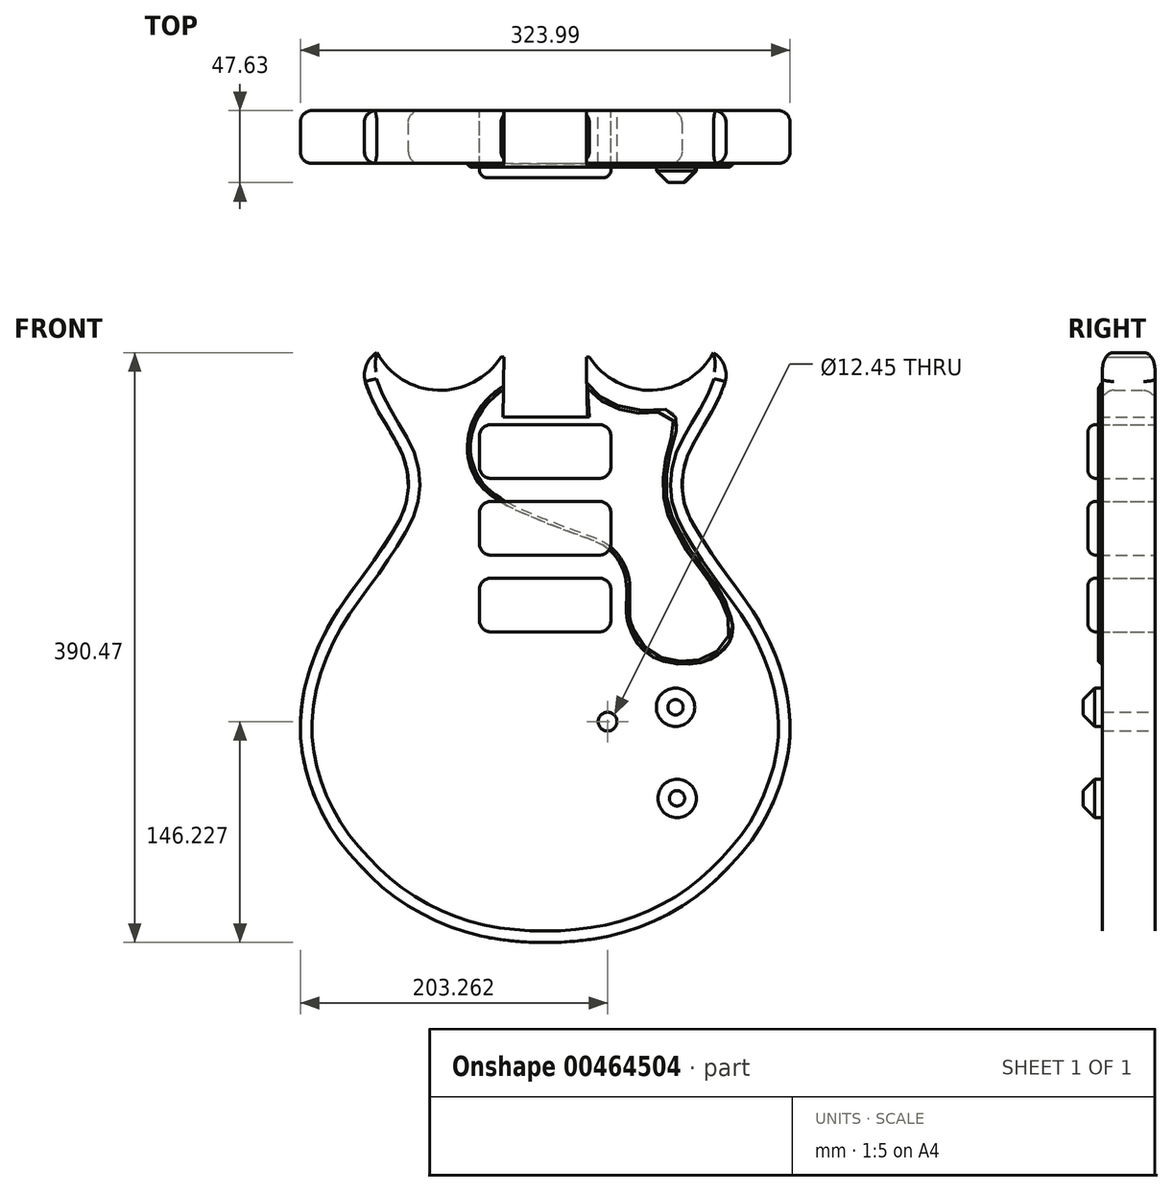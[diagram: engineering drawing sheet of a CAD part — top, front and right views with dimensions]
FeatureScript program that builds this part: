
annotation { "Feature Type Name" : "Feature", "Feature Type Description" : "" }
export const myFeature = defineFeature(function(context is Context, id is Id, definition is map)
    precondition{}
    {
        {
            var Q0;
            Q0=qCreatedBy(makeId("Front.planeOp"),FACE);
            var sketch = newSketch(context, id + "F0", { "sketchPlane" : qUnion([Q0])});
            skLineSegment(sketch, "E0", {"start": v(160.42, -4.78) * mm, "end": v(160.42, -171.98) * mm, "construction": true});
            skPoint(sketch, "E1", {"position": v(-1.5, 235.63) * mm});
            skLineSegment(sketch, "E2", {"start": v(-163.43, -5.5) * mm, "end": v(160.42, -5.5) * mm});
            skFitSpline(sketch, "E3", {"points": [v(-1.5, -151.72) * mm, v(45.27, -146.37) * mm, v(94.86, -123.83) * mm, v(121.95, -99.6) * mm, v(140.43, -76.25) * mm, v(156.45, -39.05) * mm, v(160.42, -5.5) * mm, v(154.1, 29.55) * mm, v(138.6, 63.2) * mm, v(123.42, 85.1) * mm, v(106.27, 109.26) * mm, v(94.33, 129.17) * mm, v(90.62, 138.56) * mm, v(89.22, 146.97) * mm, v(89.22, 156.81) * mm, v(91.97, 168.61) * mm, v(96.1, 177.88) * mm, v(102.04, 187.96) * mm, v(117.66, 219.62) * mm], "startDerivative": vector(474.35, 0.52) * mm, "endDerivative": vector(103.92, 419.42) * mm});
            skLineSegment(sketch, "E4", {"start": v(-1.5, 235.63) * mm, "end": v(27.7, 235.63) * mm});
            skLineSegment(sketch, "E5", {"start": v(-1.5, 235.63) * mm, "end": v(-30.71, 235.63) * mm});
            skArc(sketch, "E6", {"start": v(117.66, 219.62) * mm, "mid": v(116.83, 230.43) * mm, "end": v(109.86, 238.75) * mm});
            skArc(sketch, "E7", {"start": v(27.7, 235.63) * mm, "mid": v(69.67, 213.82) * mm, "end": v(109.86, 238.75) * mm});
            skArc(sketch, "E8.MirrorCS", {"start": v(-30.71, 235.63) * mm, "mid": v(-72.68, 213.82) * mm, "end": v(-112.87, 238.75) * mm});
            skArc(sketch, "E9.MirrorCS", {"start": v(-120.66, 219.62) * mm, "mid": v(-119.83, 230.43) * mm, "end": v(-112.87, 238.75) * mm});
            skPoint(sketch, "E10", {"position": v(-1.5, 80.55) * mm});
            skPoint(sketch, "E11", {"position": v(-1.5, 99.8) * mm});
            skPoint(sketch, "E12", {"position": v(-1.5, 175.58) * mm});
            skPoint(sketch, "E13", {"position": v(-1.5, 194.73) * mm});
            skPoint(sketch, "E14", {"position": v(109.79, 201.35) * mm});
            skPoint(sketch, "E15", {"position": v(-1.5, -5.67) * mm});
            skFitSpline(sketch, "E16.MirrorCS", {"points": [v(-1.5, -151.72) * mm, v(-48.27, -146.37) * mm, v(-97.86, -123.83) * mm, v(-122.77, -101.9) * mm, v(-143.44, -76.25) * mm, v(-159.45, -39.05) * mm, v(-163.43, -5.5) * mm, v(-157.11, 29.55) * mm, v(-141.6, 63.2) * mm, v(-126.43, 85.1) * mm, v(-109.28, 109.26) * mm, v(-97.34, 129.17) * mm, v(-93.62, 138.56) * mm, v(-92.23, 146.97) * mm, v(-92.23, 156.81) * mm, v(-94.98, 168.61) * mm, v(-99.1, 177.88) * mm, v(-105.05, 187.96) * mm, v(-120.66, 219.62) * mm], "startDerivative": vector(-474.35, 0.52) * mm, "endDerivative": vector(-103.92, 419.42) * mm});
            skPoint(sketch, "E17", {"position": v(30.82, 231.35) * mm});
            skCircle(sketch, "E18", {"center": v(-42.78, -5.5) * mm, "radius": 6.22 * mm});
            skCircle(sketch, "E19", {"center": v(39.77, -5.5) * mm, "radius": 6.22 * mm});
            skLineSegment(sketch, "E20", {"start": v(-1.5, 31.8) * mm, "end": v(-1.5, 657.27) * mm});
            skPoint(sketch, "E21", {"position": v(-1.5, 196) * mm});
            skLineSegment(sketch, "E22", {"start": v(-1.5, 196) * mm, "end": v(26.44, 196) * mm});
            skLineSegment(sketch, "E23", {"start": v(26.44, 196) * mm, "end": v(-1.5, 196) * mm});
            skLineSegment(sketch, "E24", {"start": v(-1.5, 196) * mm, "end": v(-29.44, 196) * mm});
            skLineSegment(sketch, "E25", {"start": v(-1.5, 657.27) * mm, "end": v(-22.14, 657.27) * mm});
            skLineSegment(sketch, "E26", {"start": v(-1.5, 657.27) * mm, "end": v(19.13, 657.27) * mm});
            skLineSegment(sketch, "E27", {"start": v(19.13, 657.27) * mm, "end": v(26.44, 196) * mm});
            skLineSegment(sketch, "E28", {"start": v(-29.44, 196) * mm, "end": v(-22.14, 657.27) * mm});
            skLineSegment(sketch, "E29", {"start": v(-1.5, 31.8) * mm, "end": v(87.54, 31.8) * mm});
            skLineSegment(sketch, "E30.bottom", {"start": v(-37.38, 140.28) * mm, "end": v(34.37, 140.28) * mm});
            skLineSegment(sketch, "E30.top", {"start": v(-37.38, 104.72) * mm, "end": v(34.37, 104.72) * mm});
            skLineSegment(sketch, "E30.left", {"start": v(-45, 132.66) * mm, "end": v(-45, 112.34) * mm});
            skLineSegment(sketch, "E30.right", {"start": v(42, 132.66) * mm, "end": v(42, 112.34) * mm});
            skPoint(sketch, "E31.visualSharp", {"position": v(-45, 140.28) * mm});
            skArc(sketch, "E31.filletArc", {"start": v(-37.38, 140.28) * mm, "mid": v(-42.77, 138.05) * mm, "end": v(-45, 132.66) * mm});
            skPoint(sketch, "E32.visualSharp", {"position": v(42, 140.28) * mm});
            skArc(sketch, "E32.filletArc", {"start": v(42, 132.66) * mm, "mid": v(39.76, 138.05) * mm, "end": v(34.37, 140.28) * mm});
            skPoint(sketch, "E33.visualSharp", {"position": v(42, 104.72) * mm});
            skArc(sketch, "E33.filletArc", {"start": v(34.37, 104.72) * mm, "mid": v(39.76, 106.95) * mm, "end": v(42, 112.34) * mm});
            skPoint(sketch, "E34.visualSharp", {"position": v(-45, 104.72) * mm});
            skArc(sketch, "E34.filletArc", {"start": v(-45, 112.34) * mm, "mid": v(-42.77, 106.95) * mm, "end": v(-37.38, 104.72) * mm});
            skLineSegment(sketch, "E35", {"start": v(-1.5, 140.28) * mm, "end": v(-1.5, 104.72) * mm, "construction": true});
            skLineSegment(sketch, "E36", {"start": v(-45, 122.5) * mm, "end": v(42, 122.5) * mm, "construction": true});
            skLineSegment(sketch, "E37.bottom", {"start": v(-37.38, 191.08) * mm, "end": v(34.37, 191.08) * mm});
            skLineSegment(sketch, "E37.top", {"start": v(-37.38, 155.52) * mm, "end": v(34.37, 155.52) * mm});
            skLineSegment(sketch, "E37.left", {"start": v(-45, 183.46) * mm, "end": v(-45, 163.14) * mm});
            skLineSegment(sketch, "E37.right", {"start": v(42, 183.46) * mm, "end": v(42, 163.14) * mm});
            skPoint(sketch, "E38.visualSharp", {"position": v(-45, 186.25) * mm});
            skArc(sketch, "E38.filletArc", {"start": v(-37.38, 191.08) * mm, "mid": v(-42.77, 188.85) * mm, "end": v(-45, 183.46) * mm});
            skPoint(sketch, "E39.visualSharp", {"position": v(42, 186.25) * mm});
            skArc(sketch, "E39.filletArc", {"start": v(42, 183.46) * mm, "mid": v(39.76, 188.85) * mm, "end": v(34.37, 191.08) * mm});
            skPoint(sketch, "E40.visualSharp", {"position": v(42, 155.52) * mm});
            skArc(sketch, "E40.filletArc", {"start": v(34.37, 155.52) * mm, "mid": v(39.76, 157.75) * mm, "end": v(42, 163.14) * mm});
            skPoint(sketch, "E41.visualSharp", {"position": v(-45, 155.52) * mm});
            skArc(sketch, "E41.filletArc", {"start": v(-45, 163.14) * mm, "mid": v(-42.77, 157.75) * mm, "end": v(-37.38, 155.52) * mm});
            skLineSegment(sketch, "E42", {"start": v(-1.5, 186.25) * mm, "end": v(-1.5, 150.7) * mm, "construction": true});
            skLineSegment(sketch, "E43", {"start": v(-45, 173.3) * mm, "end": v(42, 173.3) * mm, "construction": true});
            skPoint(sketch, "E44", {"position": v(-1.5, 173.3) * mm});
            skPoint(sketch, "E45", {"position": v(-1.5, 122.5) * mm});
            skLineSegment(sketch, "E46.bottom", {"start": v(-37.38, 89.48) * mm, "end": v(34.37, 89.48) * mm});
            skLineSegment(sketch, "E46.top", {"start": v(-37.38, 53.92) * mm, "end": v(34.37, 53.92) * mm});
            skLineSegment(sketch, "E46.left", {"start": v(-45, 81.86) * mm, "end": v(-45, 61.54) * mm});
            skLineSegment(sketch, "E46.right", {"start": v(42, 81.86) * mm, "end": v(42, 61.54) * mm});
            skPoint(sketch, "E47.visualSharp", {"position": v(-45, 89.48) * mm});
            skArc(sketch, "E47.filletArc", {"start": v(-37.38, 89.48) * mm, "mid": v(-42.77, 87.25) * mm, "end": v(-45, 81.86) * mm});
            skPoint(sketch, "E48.visualSharp", {"position": v(42, 89.48) * mm});
            skArc(sketch, "E48.filletArc", {"start": v(42, 81.86) * mm, "mid": v(39.76, 87.25) * mm, "end": v(34.37, 89.48) * mm});
            skPoint(sketch, "E49.visualSharp", {"position": v(42, 53.92) * mm});
            skArc(sketch, "E49.filletArc", {"start": v(34.37, 53.92) * mm, "mid": v(39.76, 56.15) * mm, "end": v(42, 61.54) * mm});
            skPoint(sketch, "E50.visualSharp", {"position": v(-45, 53.92) * mm});
            skArc(sketch, "E50.filletArc", {"start": v(-45, 61.54) * mm, "mid": v(-42.77, 56.15) * mm, "end": v(-37.38, 53.92) * mm});
            skLineSegment(sketch, "E51", {"start": v(-1.5, 89.48) * mm, "end": v(-1.5, 53.92) * mm, "construction": true});
            skLineSegment(sketch, "E52", {"start": v(-45, 71.7) * mm, "end": v(42, 71.7) * mm, "construction": true});
            skPoint(sketch, "E53", {"position": v(-1.5, 71.7) * mm});
            skLineSegment(sketch, "E54", {"start": v(-1.5, -153.09) * mm, "end": v(-1.5, 827.13) * mm, "construction": true});
            skSolve(sketch);
        }
        {
            var Q0;
            {var subQ1=sQuery(id+"F0.wireOp",EDGE,"E2");var subQ5=sQuery(id+"F0.wireOp",EDGE,"E16.MirrorCS");var subQ6=makeQuery(id+"F0.imprint","INTERSECT",VERTEX,{"derivedFrom":[subQ1,subQ5]});Q0=makeQuery(id+"F0.imprint","IMPRINT",FACE,{"disambiguationData":[TD([[makeQuery(id+"F0.imprint","IMPRINT",EDGE,{"disambiguationData":[TD([[subQ6,-1.0]])],"derivedFrom":subQ1}),-1.0]])]});}
            var Q1;
            {var subQ35=sQuery(id+"F0.wireOp",EDGE,"E6");Q1=makeQuery(id+"F0.imprint","IMPRINT",FACE,{"disambiguationData":[TD([[makeQuery(id+"F0.imprint","IMPRINT",EDGE,{"derivedFrom":subQ35}),1.0]])]});}
            var Q2;
            {var subQ0=sQuery(id+"F0.wireOp",EDGE,"E19");var subQ1=sQuery(id+"F0.wireOp",EDGE,"E2");var subQ2=makeQuery(id+"F0.imprint","INTERSECT",VERTEX,{"disambiguationData":[OD(0.0)],"derivedFrom":[subQ1,subQ0]});Q2=makeQuery(id+"F0.imprint","IMPRINT",FACE,{"disambiguationData":[TD([[makeQuery(id+"F0.imprint","IMPRINT",EDGE,{"disambiguationData":[TD([[subQ2,-1.0]])],"derivedFrom":subQ1}),-1.0]])]});}
            var Q3;
            {var subQ0=sQuery(id+"F0.wireOp",EDGE,"E19");var subQ1=sQuery(id+"F0.wireOp",EDGE,"E2");var subQ2=makeQuery(id+"F0.imprint","INTERSECT",VERTEX,{"disambiguationData":[OD(0.0)],"derivedFrom":[subQ1,subQ0]});Q3=makeQuery(id+"F0.imprint","IMPRINT",FACE,{"disambiguationData":[TD([[makeQuery(id+"F0.imprint","IMPRINT",EDGE,{"disambiguationData":[TD([[subQ2,-1.0]])],"derivedFrom":subQ1}),1.0]])]});}
            var Q4;
            {var subQ0=sQuery(id+"F0.wireOp",EDGE,"E18");var subQ1=sQuery(id+"F0.wireOp",EDGE,"E2");var subQ2=makeQuery(id+"F0.imprint","INTERSECT",VERTEX,{"disambiguationData":[OD(0.0)],"derivedFrom":[subQ1,subQ0]});Q4=makeQuery(id+"F0.imprint","IMPRINT",FACE,{"disambiguationData":[TD([[makeQuery(id+"F0.imprint","IMPRINT",EDGE,{"disambiguationData":[TD([[subQ2,-1.0]])],"derivedFrom":subQ1}),-1.0]])]});}
            var Q5;
            {var subQ0=sQuery(id+"F0.wireOp",EDGE,"E18");var subQ1=sQuery(id+"F0.wireOp",EDGE,"E2");var subQ2=makeQuery(id+"F0.imprint","INTERSECT",VERTEX,{"disambiguationData":[OD(0.0)],"derivedFrom":[subQ1,subQ0]});Q5=makeQuery(id+"F0.imprint","IMPRINT",FACE,{"disambiguationData":[TD([[makeQuery(id+"F0.imprint","IMPRINT",EDGE,{"disambiguationData":[TD([[subQ2,-1.0]])],"derivedFrom":subQ1}),1.0]])]});}
            var Q6;
            Q6=makeQuery(id+"F0.imprint","IMPRINT",FACE,{"disambiguationData":[TD([[makeQuery(id+"F0.imprint","IMPRINT",EDGE,{"derivedFrom":sQuery(id+"F0.wireOp",EDGE,"E46.left")}),1.0]])]});
            var Q7;
            Q7=makeQuery(id+"F0.imprint","IMPRINT",FACE,{"disambiguationData":[TD([[makeQuery(id+"F0.imprint","IMPRINT",EDGE,{"derivedFrom":sQuery(id+"F0.wireOp",EDGE,"E46.right")}),-1.0]])]});
            var Q8;
            Q8=makeQuery(id+"F0.imprint","IMPRINT",FACE,{"disambiguationData":[TD([[makeQuery(id+"F0.imprint","IMPRINT",EDGE,{"derivedFrom":sQuery(id+"F0.wireOp",EDGE,"E30.left")}),1.0]])]});
            var Q9;
            Q9=makeQuery(id+"F0.imprint","IMPRINT",FACE,{"disambiguationData":[TD([[makeQuery(id+"F0.imprint","IMPRINT",EDGE,{"derivedFrom":sQuery(id+"F0.wireOp",EDGE,"E30.right")}),-1.0]])]});
            var Q10;
            Q10=makeQuery(id+"F0.imprint","IMPRINT",FACE,{"disambiguationData":[TD([[makeQuery(id+"F0.imprint","IMPRINT",EDGE,{"derivedFrom":sQuery(id+"F0.wireOp",EDGE,"E37.right")}),-1.0]])]});
            var Q11;
            Q11=makeQuery(id+"F0.imprint","IMPRINT",FACE,{"disambiguationData":[TD([[makeQuery(id+"F0.imprint","IMPRINT",EDGE,{"derivedFrom":sQuery(id+"F0.wireOp",EDGE,"E37.left")}),1.0]])]});
            extrude(context, id + "F1", {"entities" : qUnion([Q0, Q1, Q2, Q3, Q4, Q5, Q6, Q7, Q8, Q9, Q10, Q11]), "depth" : 34.92 * mm});
        }
        {
            var Q0;
            Q0=makeQuery(id+"F1.opExtrude","CAP_EDGE",EDGE,{"disambiguationData":[OSD([sQuery(id+"F0.wireOp",EDGE,"E3")])],"isStart":true});
            var Q1;
            Q1=makeQuery(id+"F1.opExtrude","CAP_EDGE",EDGE,{"disambiguationData":[OSD([sQuery(id+"F0.wireOp",EDGE,"E16.MirrorCS")])],"isStart":true});
            var Q2;
            Q2=makeQuery(id+"F1.opExtrude","CAP_EDGE",EDGE,{"disambiguationData":[OSD([sQuery(id+"F0.wireOp",EDGE,"E9.MirrorCS")])],"isStart":true});
            var Q3;
            Q3=makeQuery(id+"F1.opExtrude","CAP_EDGE",EDGE,{"disambiguationData":[OSD([sQuery(id+"F0.wireOp",EDGE,"E6")])],"isStart":true});
            var Q4;
            Q4=makeQuery(id+"F1.opExtrude","CAP_EDGE",EDGE,{"disambiguationData":[OSD([sQuery(id+"F0.wireOp",EDGE,"E8.MirrorCS")])],"isStart":true});
            var Q5;
            Q5=makeQuery(id+"F1.opExtrude","CAP_EDGE",EDGE,{"disambiguationData":[OSD([sQuery(id+"F0.wireOp",EDGE,"E7")])],"isStart":true});
            var Q6;
            Q6=makeQuery(id+"F1.opExtrude","CAP_EDGE",EDGE,{"disambiguationData":[OSD([sQuery(id+"F0.wireOp",EDGE,"E16.MirrorCS")])],"isStart":false});
            var Q7;
            Q7=makeQuery(id+"F1.opExtrude","CAP_EDGE",EDGE,{"disambiguationData":[OSD([sQuery(id+"F0.wireOp",EDGE,"E3")])],"isStart":false});
            var Q8;
            Q8=makeQuery(id+"F1.opExtrude","CAP_EDGE",EDGE,{"disambiguationData":[OSD([sQuery(id+"F0.wireOp",EDGE,"E6")])],"isStart":false});
            var Q9;
            Q9=makeQuery(id+"F1.opExtrude","CAP_EDGE",EDGE,{"disambiguationData":[OSD([sQuery(id+"F0.wireOp",EDGE,"E7")])],"isStart":false});
            var Q10;
            Q10=makeQuery(id+"F1.opExtrude","CAP_EDGE",EDGE,{"disambiguationData":[OSD([sQuery(id+"F0.wireOp",EDGE,"E8.MirrorCS")])],"isStart":false});
            var Q11;
            Q11=makeQuery(id+"F1.opExtrude","CAP_EDGE",EDGE,{"disambiguationData":[OSD([sQuery(id+"F0.wireOp",EDGE,"E9.MirrorCS")])],"isStart":false});
            fillet(context, id + "F2", {"entities" : qUnion([Q0, Q1, Q2, Q3, Q4, Q5, Q6, Q7, Q8, Q9, Q10, Q11]), "radius" : 7.62 * mm, "tangentPropagation" : true, "allowEdgeOverflow" : false});
        }
        {
            var Q0;
            Q0=makeQuery(id+"F1.opExtrude","CAP_FACE",FACE,{"disambiguationData":[OSD([sQuery(id+"F0.wireOp",EDGE,"E3"),sQuery(id+"F0.wireOp",EDGE,"E4"),sQuery(id+"F0.wireOp",EDGE,"E5"),sQuery(id+"F0.wireOp",EDGE,"E6"),sQuery(id+"F0.wireOp",EDGE,"E7"),sQuery(id+"F0.wireOp",EDGE,"E8.MirrorCS"),sQuery(id+"F0.wireOp",EDGE,"E9.MirrorCS"),sQuery(id+"F0.wireOp",EDGE,"E16.MirrorCS")])],"isStart":false});
            var sketch = newSketch(context, id + "F3", { "sketchPlane" : qUnion([Q0])});
            skCircle(sketch, "E55", {"center": v(84.75, 4.03) * mm, "radius": 12.7 * mm});
            skLineSegment(sketch, "E56", {"start": v(-28.67, 196.2) * mm, "end": v(27.64, 196.2) * mm});
            skLineSegment(sketch, "E57", {"start": v(27.64, 196.2) * mm, "end": v(-28.67, 196.2) * mm});
            skLineSegment(sketch, "E58", {"start": v(-28.67, 196.2) * mm, "end": v(-28.09, 217.18) * mm});
            skLineSegment(sketch, "E59", {"start": v(27.64, 196.2) * mm, "end": v(26.21, 218.58) * mm});
            skFitSpline(sketch, "E60", {"points": [v(-28.09, 217.18) * mm, v(-32, 214.68) * mm, v(-38.15, 209.37) * mm, v(-43.19, 203.89) * mm, v(-47.7, 196.71) * mm, v(-49.69, 192.69) * mm, v(-51.47, 186.97) * mm, v(-52.46, 182.4) * mm, v(-52.88, 172.89) * mm, v(-50.71, 162.59) * mm, v(-47.7, 155.96) * mm, v(-42.9, 149.19) * mm, v(-34.02, 141.94) * mm, v(-21.88, 134.98) * mm, v(12.12, 121.06) * mm, v(18.75, 118.66) * mm, v(29.94, 114.48) * mm, v(38.38, 110.17) * mm, v(44.5, 104.58) * mm, v(47.07, 100.85) * mm, v(49.74, 95.8) * mm, v(52.13, 86.88) * mm, v(52.26, 70.92) * mm, v(55.39, 54.15) * mm], "startDerivative": vector(-124.22, -71.5) * mm, "endDerivative": vector(159.25, -326.32) * mm});
            skFitSpline(sketch, "E61", {"points": [v(26.21, 218.58) * mm, v(33.66, 210.6) * mm, v(44.04, 204.75) * mm, v(60.98, 200.63) * mm, v(78.94, 201.16) * mm, v(83.6, 198.1) * mm, v(85.59, 193.05) * mm, v(85.45, 187.73) * mm, v(80.8, 171.23) * mm, v(78.7, 157.11) * mm, v(79.14, 141.45) * mm, v(82.39, 130.15) * mm, v(87.65, 119.97) * mm, v(92.8, 110.24) * mm, v(101.77, 98.05) * mm, v(109.75, 86.88) * mm, v(116.5, 76) * mm, v(122.52, 58.67) * mm, v(121.54, 49.61) * mm, v(117.29, 42.9) * mm, v(110.13, 37.2) * mm, v(97.94, 32.83) * mm, v(76.8, 34.4) * mm, v(63.25, 41.99) * mm, v(57.12, 50.33) * mm, v(55.39, 54.15) * mm], "startDerivative": vector(150.4, -175.72) * mm, "endDerivative": vector(-62.53, 202.68) * mm});
            skLineSegment(sketch, "E62.bottom", {"start": v(293.55, 165.04) * mm, "end": v(365.3, 165.04) * mm});
            skLineSegment(sketch, "E62.top", {"start": v(293.55, 129.48) * mm, "end": v(365.3, 129.48) * mm});
            skLineSegment(sketch, "E62.left", {"start": v(285.93, 157.42) * mm, "end": v(285.93, 137.1) * mm});
            skLineSegment(sketch, "E62.right", {"start": v(372.92, 157.42) * mm, "end": v(372.92, 137.1) * mm});
            skPoint(sketch, "E63.visualSharp", {"position": v(285.93, 165.04) * mm});
            skArc(sketch, "E63.filletArc", {"start": v(293.55, 165.04) * mm, "mid": v(288.16, 162.8) * mm, "end": v(285.93, 157.42) * mm});
            skPoint(sketch, "E64.visualSharp", {"position": v(372.92, 165.04) * mm});
            skArc(sketch, "E64.filletArc", {"start": v(372.92, 157.42) * mm, "mid": v(370.7, 162.8) * mm, "end": v(365.3, 165.04) * mm});
            skPoint(sketch, "E65.visualSharp", {"position": v(372.92, 129.48) * mm});
            skArc(sketch, "E65.filletArc", {"start": v(365.3, 129.48) * mm, "mid": v(370.7, 131.7) * mm, "end": v(372.92, 137.1) * mm});
            skPoint(sketch, "E66.visualSharp", {"position": v(285.93, 129.48) * mm});
            skArc(sketch, "E66.filletArc", {"start": v(285.93, 137.1) * mm, "mid": v(288.16, 131.7) * mm, "end": v(293.55, 129.48) * mm});
            skLineSegment(sketch, "E67", {"start": v(329.42, 165.04) * mm, "end": v(329.42, 129.48) * mm, "construction": true});
            skLineSegment(sketch, "E68", {"start": v(285.93, 147.26) * mm, "end": v(372.92, 147.26) * mm, "construction": true});
            skLineSegment(sketch, "E69.bottom", {"start": v(468.44, 149.86) * mm, "end": v(540.2, 149.86) * mm});
            skLineSegment(sketch, "E69.top", {"start": v(468.44, 114.3) * mm, "end": v(540.2, 114.3) * mm});
            skLineSegment(sketch, "E69.left", {"start": v(460.82, 142.24) * mm, "end": v(460.82, 121.92) * mm});
            skLineSegment(sketch, "E69.right", {"start": v(547.82, 142.24) * mm, "end": v(547.82, 121.92) * mm});
            skPoint(sketch, "E70.visualSharp", {"position": v(460.82, 149.86) * mm});
            skArc(sketch, "E70.filletArc", {"start": v(468.44, 149.86) * mm, "mid": v(463.05, 147.63) * mm, "end": v(460.82, 142.24) * mm});
            skPoint(sketch, "E71.visualSharp", {"position": v(547.82, 149.86) * mm});
            skArc(sketch, "E71.filletArc", {"start": v(547.82, 142.24) * mm, "mid": v(545.58, 147.63) * mm, "end": v(540.2, 149.86) * mm});
            skPoint(sketch, "E72.visualSharp", {"position": v(547.82, 114.3) * mm});
            skArc(sketch, "E72.filletArc", {"start": v(540.2, 114.3) * mm, "mid": v(545.58, 116.53) * mm, "end": v(547.82, 121.92) * mm});
            skPoint(sketch, "E73.visualSharp", {"position": v(460.82, 114.3) * mm});
            skArc(sketch, "E73.filletArc", {"start": v(460.82, 121.92) * mm, "mid": v(463.05, 116.53) * mm, "end": v(468.44, 114.3) * mm});
            skLineSegment(sketch, "E74", {"start": v(504.32, 149.86) * mm, "end": v(504.32, 114.3) * mm, "construction": true});
            skLineSegment(sketch, "E75", {"start": v(460.82, 132.08) * mm, "end": v(547.82, 132.08) * mm, "construction": true});
            skLineSegment(sketch, "E76.bottom", {"start": v(468.44, 200.66) * mm, "end": v(540.2, 200.66) * mm});
            skLineSegment(sketch, "E76.top", {"start": v(468.44, 165.1) * mm, "end": v(540.2, 165.1) * mm});
            skLineSegment(sketch, "E76.left", {"start": v(460.82, 193.04) * mm, "end": v(460.82, 172.72) * mm});
            skLineSegment(sketch, "E76.right", {"start": v(547.82, 193.04) * mm, "end": v(547.82, 172.72) * mm});
            skPoint(sketch, "E77.visualSharp", {"position": v(460.82, 200.66) * mm});
            skArc(sketch, "E77.filletArc", {"start": v(468.44, 200.66) * mm, "mid": v(463.05, 198.43) * mm, "end": v(460.82, 193.04) * mm});
            skPoint(sketch, "E78.visualSharp", {"position": v(547.82, 200.66) * mm});
            skArc(sketch, "E78.filletArc", {"start": v(547.82, 193.04) * mm, "mid": v(545.58, 198.43) * mm, "end": v(540.2, 200.66) * mm});
            skPoint(sketch, "E79.visualSharp", {"position": v(547.82, 165.1) * mm});
            skArc(sketch, "E79.filletArc", {"start": v(540.2, 165.1) * mm, "mid": v(545.58, 167.33) * mm, "end": v(547.82, 172.72) * mm});
            skPoint(sketch, "E80.visualSharp", {"position": v(460.82, 165.1) * mm});
            skArc(sketch, "E80.filletArc", {"start": v(460.82, 172.72) * mm, "mid": v(463.05, 167.33) * mm, "end": v(468.44, 165.1) * mm});
            skLineSegment(sketch, "E81", {"start": v(504.32, 200.66) * mm, "end": v(504.32, 165.1) * mm, "construction": true});
            skLineSegment(sketch, "E82", {"start": v(460.82, 182.88) * mm, "end": v(547.82, 182.88) * mm, "construction": true});
            skPoint(sketch, "E83", {"position": v(504.32, 182.88) * mm});
            skPoint(sketch, "E84", {"position": v(504.32, 132.08) * mm});
            skPoint(sketch, "E85", {"position": v(329.42, 147.26) * mm});
            skLineSegment(sketch, "E86", {"start": v(504.32, 439.48) * mm, "end": v(504.32, 14.4) * mm, "construction": true});
            skLineSegment(sketch, "E87.bottom", {"start": v(468.44, 99.06) * mm, "end": v(540.2, 99.06) * mm});
            skLineSegment(sketch, "E87.top", {"start": v(468.44, 63.5) * mm, "end": v(540.2, 63.5) * mm});
            skLineSegment(sketch, "E87.left", {"start": v(460.82, 91.44) * mm, "end": v(460.82, 71.12) * mm});
            skLineSegment(sketch, "E87.right", {"start": v(547.82, 91.44) * mm, "end": v(547.82, 71.12) * mm});
            skPoint(sketch, "E88.visualSharp", {"position": v(460.82, 99.06) * mm});
            skArc(sketch, "E88.filletArc", {"start": v(468.44, 99.06) * mm, "mid": v(463.05, 96.83) * mm, "end": v(460.82, 91.44) * mm});
            skPoint(sketch, "E89.visualSharp", {"position": v(547.82, 99.06) * mm});
            skArc(sketch, "E89.filletArc", {"start": v(547.82, 91.44) * mm, "mid": v(545.58, 96.83) * mm, "end": v(540.2, 99.06) * mm});
            skPoint(sketch, "E90.visualSharp", {"position": v(547.82, 63.5) * mm});
            skArc(sketch, "E90.filletArc", {"start": v(540.2, 63.5) * mm, "mid": v(545.58, 65.73) * mm, "end": v(547.82, 71.12) * mm});
            skPoint(sketch, "E91.visualSharp", {"position": v(460.82, 63.5) * mm});
            skArc(sketch, "E91.filletArc", {"start": v(460.82, 71.12) * mm, "mid": v(463.05, 65.73) * mm, "end": v(468.44, 63.5) * mm});
            skLineSegment(sketch, "E92", {"start": v(504.32, 99.06) * mm, "end": v(504.32, 63.5) * mm, "construction": true});
            skLineSegment(sketch, "E93", {"start": v(460.82, 81.28) * mm, "end": v(547.82, 81.28) * mm, "construction": true});
            skPoint(sketch, "E94", {"position": v(504.32, 81.28) * mm});
            skPoint(sketch, "E95", {"position": v(-1.5, 235.63) * mm});
            skCircle(sketch, "E96", {"center": v(129.28, 16.9) * mm, "radius": 7.33 * mm});
            skCircle(sketch, "E97", {"center": v(85.75, -56.3) * mm, "radius": 12.7 * mm});
            skSolve(sketch);
        }
        {
            var Q0;
            Q0=makeQuery(id+"F3.imprint","IMPRINT",FACE,{"disambiguationData":[TD([[makeQuery(id+"F3.imprint","IMPRINT",EDGE,{"derivedFrom":sQuery(id+"F3.wireOp",EDGE,"E57")}),1.0]])]});
            var Q1;
            {var subQ2=sQuery(id+"F3.wireOp",EDGE,"E59");Q1=makeQuery(id+"F3.imprint","IMPRINT",FACE,{"disambiguationData":[TD([[makeQuery(id+"F3.imprint","IMPRINT",EDGE,{"derivedFrom":subQ2}),-1.0]])]});}
            extrude(context, id + "F4", {"entities" : qUnion([Q0, Q1]), "operationType" : NewBodyOperationType.ADD, "depth" : 2.54 * mm});
        }
        {
            var Q0;
            {var subQ0=sQuery(id+"F3.wireOp",EDGE,"E60");Q0=makeQuery(id+"F4.opExtrude","CAP_EDGE",EDGE,{"disambiguationData":[OSD([subQ0]),TDD([makeQuery(id+"F3.imprint","IMPRINT",EDGE,{"disambiguationData":[TD([[makeQuery(id+"F3.imprint","INTERSECT",VERTEX,{"derivedFrom":[subQ0,sQuery(id+"F3.wireOp",EDGE,"E61")]}),1.0]])],"derivedFrom":subQ0})])],"isStart":false});}
            var Q1;
            Q1=makeQuery(id+"F4.opExtrude","CAP_EDGE",EDGE,{"disambiguationData":[OSD([sQuery(id+"F3.wireOp",EDGE,"E61")])],"isStart":false});
            var Q2;
            {var subQ0=sQuery(id+"F3.wireOp",EDGE,"E60");Q2=makeQuery(id+"F4.opExtrude","CAP_EDGE",EDGE,{"disambiguationData":[OSD([subQ0]),TDD([makeQuery(id+"F3.imprint","IMPRINT",EDGE,{"disambiguationData":[TD([[makeQuery(id+"F3.imprint","INTERSECT",VERTEX,{"derivedFrom":[sQuery(id+"F3.wireOp",EDGE,"E58"),subQ0]}),-1.0]])],"derivedFrom":subQ0})])],"isStart":false});}
            chamfer(context, id + "F5", {"entities" : qUnion([Q0, Q1, Q2]), "width" : 2.03 * mm, "tangentPropagation" : true});
        }
        {
            var Q0;
            Q0=makeQuery(id+"F3.imprint","IMPRINT",FACE,{"disambiguationData":[TD([[makeQuery(id+"F3.imprint","IMPRINT",EDGE,{"derivedFrom":sQuery(id+"F3.wireOp",EDGE,"E55")}),1.0]])]});
            var Q1;
            Q1=makeQuery(id+"F3.imprint","IMPRINT",FACE,{"disambiguationData":[TD([[makeQuery(id+"F3.imprint","IMPRINT",EDGE,{"derivedFrom":sQuery(id+"F3.wireOp",EDGE,"E97")}),1.0]])]});
            extrude(context, id + "F6", {"entities" : qUnion([Q0, Q1]), "depth" : 12.7 * mm});
        }
        {
            var Q0;
            Q0=makeQuery(id+"F6.opExtrude","CAP_EDGE",EDGE,{"disambiguationData":[OSD([sQuery(id+"F3.wireOp",EDGE,"E55")])],"isStart":false});
            var Q1;
            Q1=makeQuery(id+"F6.opExtrude","CAP_EDGE",EDGE,{"disambiguationData":[OSD([sQuery(id+"F3.wireOp",EDGE,"E97")])],"isStart":false});
            chamfer(context, id + "F7", {"entities" : qUnion([Q0, Q1]), "width" : 7.62 * mm, "tangentPropagation" : true});
        }
        {
            var Q0;
            Q0=makeQuery(id+"F0.imprint","IMPRINT",FACE,{"disambiguationData":[TD([[makeQuery(id+"F0.imprint","IMPRINT",EDGE,{"derivedFrom":sQuery(id+"F0.wireOp",EDGE,"E46.left")}),1.0]])]});
            var Q1;
            Q1=makeQuery(id+"F0.imprint","IMPRINT",FACE,{"disambiguationData":[TD([[makeQuery(id+"F0.imprint","IMPRINT",EDGE,{"derivedFrom":sQuery(id+"F0.wireOp",EDGE,"E46.right")}),-1.0]])]});
            var Q2;
            Q2=makeQuery(id+"F0.imprint","IMPRINT",FACE,{"disambiguationData":[TD([[makeQuery(id+"F0.imprint","IMPRINT",EDGE,{"derivedFrom":sQuery(id+"F0.wireOp",EDGE,"E30.right")}),-1.0]])]});
            var Q3;
            Q3=makeQuery(id+"F0.imprint","IMPRINT",FACE,{"disambiguationData":[TD([[makeQuery(id+"F0.imprint","IMPRINT",EDGE,{"derivedFrom":sQuery(id+"F0.wireOp",EDGE,"E30.left")}),1.0]])]});
            var Q4;
            Q4=makeQuery(id+"F0.imprint","IMPRINT",FACE,{"disambiguationData":[TD([[makeQuery(id+"F0.imprint","IMPRINT",EDGE,{"derivedFrom":sQuery(id+"F0.wireOp",EDGE,"E37.left")}),1.0]])]});
            var Q5;
            Q5=makeQuery(id+"F0.imprint","IMPRINT",FACE,{"disambiguationData":[TD([[makeQuery(id+"F0.imprint","IMPRINT",EDGE,{"derivedFrom":sQuery(id+"F0.wireOp",EDGE,"E37.right")}),-1.0]])]});
            extrude(context, id + "F8", {"entities" : qUnion([Q0, Q1, Q2, Q3, Q4, Q5]), "depth" : 44.45 * mm});
        }
        {
            var Q0;
            Q0=makeQuery(id+"F8.opExtrude","CAP_EDGE",EDGE,{"disambiguationData":[OSD([sQuery(id+"F0.wireOp",EDGE,"E46.top")])],"isStart":false});
            var Q1;
            Q1=makeQuery(id+"F8.opExtrude","CAP_EDGE",EDGE,{"disambiguationData":[OSD([sQuery(id+"F0.wireOp",EDGE,"E30.top")])],"isStart":false});
            var Q2;
            Q2=makeQuery(id+"F8.opExtrude","CAP_EDGE",EDGE,{"disambiguationData":[OSD([sQuery(id+"F0.wireOp",EDGE,"E37.top")])],"isStart":false});
            fillet(context, id + "F9", {"entities" : qUnion([Q0, Q1, Q2]), "radius" : 5.08 * mm, "tangentPropagation" : true, "allowEdgeOverflow" : false});
        }
    });
